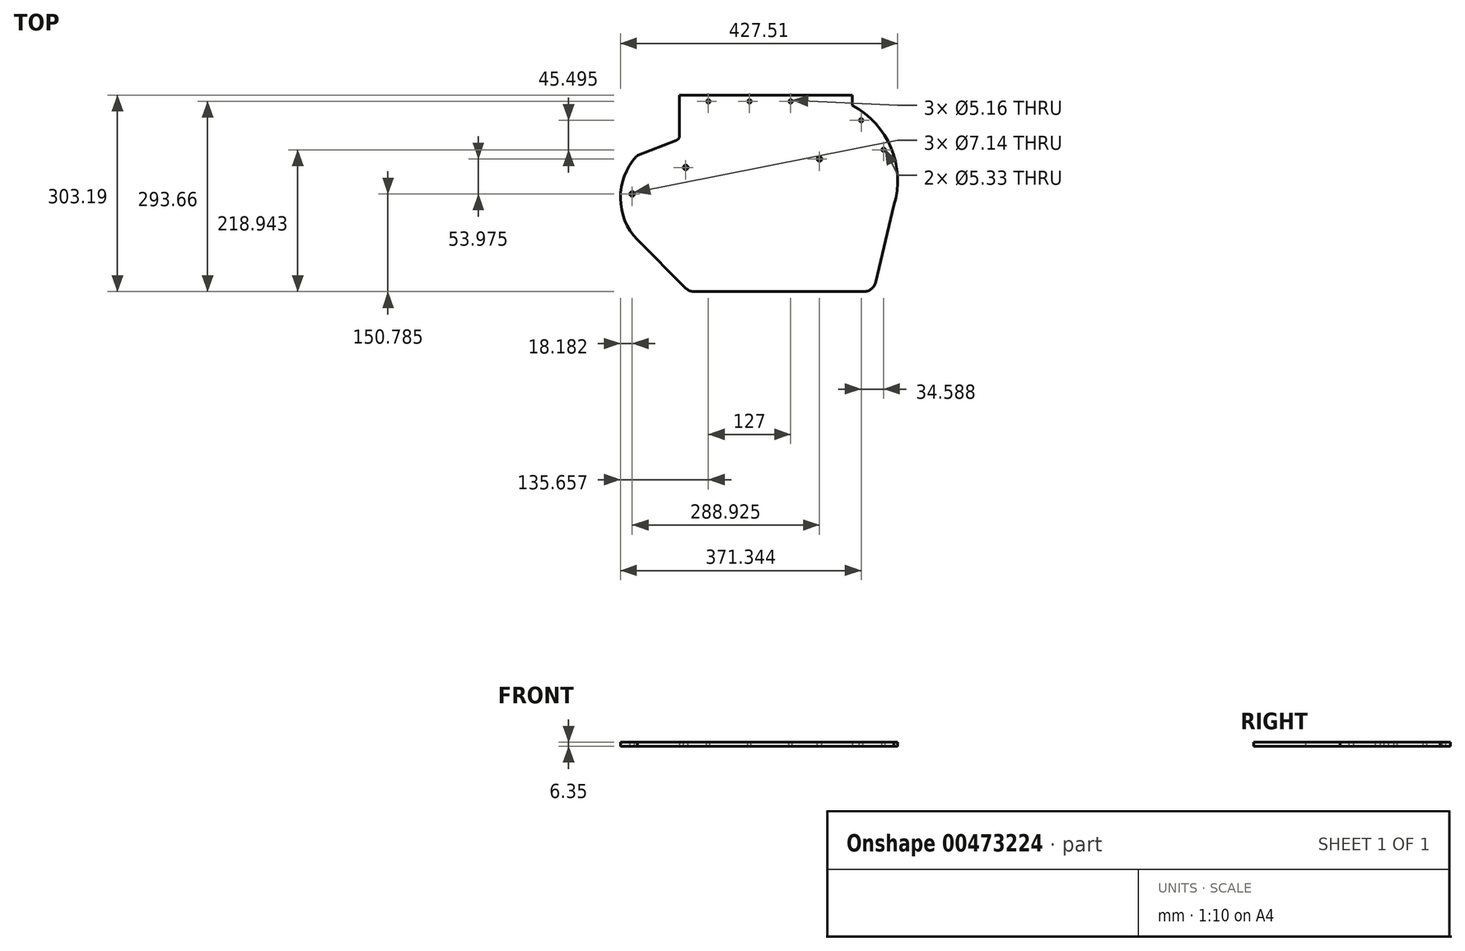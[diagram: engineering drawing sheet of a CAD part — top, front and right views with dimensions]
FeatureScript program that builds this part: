
annotation { "Feature Type Name" : "Feature", "Feature Type Description" : "" }
export const myFeature = defineFeature(function(context is Context, id is Id, definition is map)
    precondition{}
    {
        {
            var Q0;
            Q0=qCreatedBy(makeId("Top.planeOp"),FACE);
            var sketch = newSketch(context, id + "F0", { "sketchPlane" : qUnion([Q0])});
            skLineSegment(sketch, "E0", {"start": v(89.9, 293.19) * mm, "end": v(89.9, 230.84) * mm});
            skLineSegment(sketch, "E1", {"start": v(84.87, 223.45) * mm, "end": v(25.61, 200.17) * mm});
            skLineSegment(sketch, "E2", {"start": v(24.78, 70.08) * mm, "end": v(99.28, -4.42) * mm});
            skLineSegment(sketch, "E3", {"start": v(112.75, -10) * mm, "end": v(373.81, -10) * mm});
            skLineSegment(sketch, "E4", {"start": v(392.34, 4.64) * mm, "end": v(420.6, 123.35) * mm});
            skLineSegment(sketch, "E5", {"start": v(89.9, 293.19) * mm, "end": v(356.6, 293.19) * mm});
            skLineSegment(sketch, "E6", {"start": v(356.6, 293.19) * mm, "end": v(356.6, 277.31) * mm});
            skPoint(sketch, "E7.visualSharp", {"position": v(89.9, 225.43) * mm});
            skArc(sketch, "E7.filletArc", {"start": v(84.87, 223.45) * mm, "mid": v(88.53, 226.37) * mm, "end": v(89.9, 230.84) * mm});
            skPoint(sketch, "E8.startSnap0", {"position": v(0, 142.48) * mm});
            skArc(sketch, "E9.0", {"start": v(23.24, 198.54) * mm, "mid": v(-1.3, 134) * mm, "end": v(24.78, 70.08) * mm});
            skPoint(sketch, "E10.visualSharp", {"position": v(104.85, -10) * mm});
            skArc(sketch, "E10.filletArc", {"start": v(99.28, -4.42) * mm, "mid": v(105.46, -8.55) * mm, "end": v(112.75, -10) * mm});
            skPoint(sketch, "E11.visualSharp", {"position": v(388.86, -10) * mm});
            skArc(sketch, "E11.filletArc", {"start": v(373.81, -10) * mm, "mid": v(385.62, -5.9) * mm, "end": v(392.34, 4.64) * mm});
            skArc(sketch, "E12", {"start": v(420.6, 123.35) * mm, "mid": v(416.15, 211.78) * mm, "end": v(356.6, 277.31) * mm});
            skPoint(sketch, "E13.visualSharp", {"position": v(24.26, 199.64) * mm});
            skArc(sketch, "E13.filletArc", {"start": v(25.61, 200.17) * mm, "mid": v(24.33, 199.49) * mm, "end": v(23.24, 198.54) * mm});
            skSolve(sketch);
        }
        {
            var Q0;
            Q0=makeQuery(id+"F0.imprint","IMPRINT",FACE,{"disambiguationData":[TD([[makeQuery(id+"F0.imprint","IMPRINT",EDGE,{"derivedFrom":sQuery(id+"F0.wireOp",EDGE,"E0")}),1.0]])]});
            extrude(context, id + "F1", {"entities" : qUnion([Q0]), "depth" : 6.35 * mm});
        }
        {
            var Q0;
            Q0=makeQuery(id+"F1.opExtrude","CAP_FACE",FACE,{"disambiguationData":[OSD([sQuery(id+"F0.wireOp",EDGE,"E0"),sQuery(id+"F0.wireOp",EDGE,"E1"),sQuery(id+"F0.wireOp",EDGE,"E2"),sQuery(id+"F0.wireOp",EDGE,"E3"),sQuery(id+"F0.wireOp",EDGE,"E4"),sQuery(id+"F0.wireOp",EDGE,"E5"),sQuery(id+"F0.wireOp",EDGE,"E6"),sQuery(id+"F0.wireOp",EDGE,"E7.filletArc"),sQuery(id+"F0.wireOp",EDGE,"E9.0"),sQuery(id+"F0.wireOp",EDGE,"E10.filletArc"),sQuery(id+"F0.wireOp",EDGE,"E11.filletArc"),sQuery(id+"F0.wireOp",EDGE,"E12")])],"isStart":false});
            var sketch = newSketch(context, id + "F2", { "sketchPlane" : qUnion([Q0])});
            skCircle(sketch, "E14", {"center": v(261.36, 283.66) * mm, "radius": 2.58 * mm});
            skCircle(sketch, "E15", {"center": v(197.86, 283.66) * mm, "radius": 2.58 * mm});
            skCircle(sketch, "E16", {"center": v(134.36, 283.66) * mm, "radius": 2.58 * mm});
            skSolve(sketch);
        }
        {
            var Q0;
            Q0 = qSketchRegion(id + "F2", true);
            extrude(context, id + "F3", {"entities" : qUnion([Q0]), "operationType" : NewBodyOperationType.REMOVE, "endBound" : BoundingType.UP_TO_NEXT, "oppositeDirection" : true, "depth" : 25.4 * mm});
        }
        {
            var Q0;
            Q0=makeQuery(id+"F1.opExtrude","CAP_FACE",FACE,{"disambiguationData":[OSD([sQuery(id+"F0.wireOp",EDGE,"E0"),sQuery(id+"F0.wireOp",EDGE,"E1"),sQuery(id+"F0.wireOp",EDGE,"E2"),sQuery(id+"F0.wireOp",EDGE,"E3"),sQuery(id+"F0.wireOp",EDGE,"E4"),sQuery(id+"F0.wireOp",EDGE,"E5"),sQuery(id+"F0.wireOp",EDGE,"E6"),sQuery(id+"F0.wireOp",EDGE,"E7.filletArc"),sQuery(id+"F0.wireOp",EDGE,"E9.0"),sQuery(id+"F0.wireOp",EDGE,"E10.filletArc"),sQuery(id+"F0.wireOp",EDGE,"E11.filletArc"),sQuery(id+"F0.wireOp",EDGE,"E12"),sQuery(id+"F0.wireOp",EDGE,"E13.filletArc")])],"isStart":false});
            var sketch = newSketch(context, id + "F4", { "sketchPlane" : qUnion([Q0])});
            skCircle(sketch, "E17", {"center": v(99.43, 181.66) * mm, "radius": 3.57 * mm});
            skCircle(sketch, "E18", {"center": v(16.88, 140.79) * mm, "radius": 3.57 * mm});
            skCircle(sketch, "E19", {"center": v(305.8, 194.76) * mm, "radius": 3.57 * mm});
            skSolve(sketch);
        }
        {
            var Q0;
            Q0 = qSketchRegion(id + "F4", true);
            extrude(context, id + "F5", {"entities" : qUnion([Q0]), "operationType" : NewBodyOperationType.REMOVE, "oppositeDirection" : true, "depth" : 9.52 * mm, "offsetDistance" : 25.4 * mm});
        }
        {
            var Q0;
            Q0=makeQuery(id+"F1.opExtrude","CAP_FACE",FACE,{"disambiguationData":[OSD([sQuery(id+"F0.wireOp",EDGE,"E0"),sQuery(id+"F0.wireOp",EDGE,"E1"),sQuery(id+"F0.wireOp",EDGE,"E2"),sQuery(id+"F0.wireOp",EDGE,"E3"),sQuery(id+"F0.wireOp",EDGE,"E4"),sQuery(id+"F0.wireOp",EDGE,"E5"),sQuery(id+"F0.wireOp",EDGE,"E6"),sQuery(id+"F0.wireOp",EDGE,"E7.filletArc"),sQuery(id+"F0.wireOp",EDGE,"E9.0"),sQuery(id+"F0.wireOp",EDGE,"E10.filletArc"),sQuery(id+"F0.wireOp",EDGE,"E11.filletArc"),sQuery(id+"F0.wireOp",EDGE,"E12"),sQuery(id+"F0.wireOp",EDGE,"E13.filletArc")])],"isStart":false});
            var sketch = newSketch(context, id + "F6", { "sketchPlane" : qUnion([Q0])});
            skCircle(sketch, "E20", {"center": v(370.04, 254.44) * mm, "radius": 2.67 * mm});
            skCircle(sketch, "E21", {"center": v(404.63, 208.94) * mm, "radius": 2.67 * mm});
            skSolve(sketch);
        }
        {
            var Q0;
            Q0 = qSketchRegion(id + "F6", true);
            extrude(context, id + "F7", {"entities" : qUnion([Q0]), "operationType" : NewBodyOperationType.REMOVE, "flatOperationType" : FlatOperationType.REMOVE, "oppositeDirection" : true, "depth" : 7.62 * mm, "offsetDistance" : 25.4 * mm, "domain" : OperationDomain.MODEL});
        }
    });
